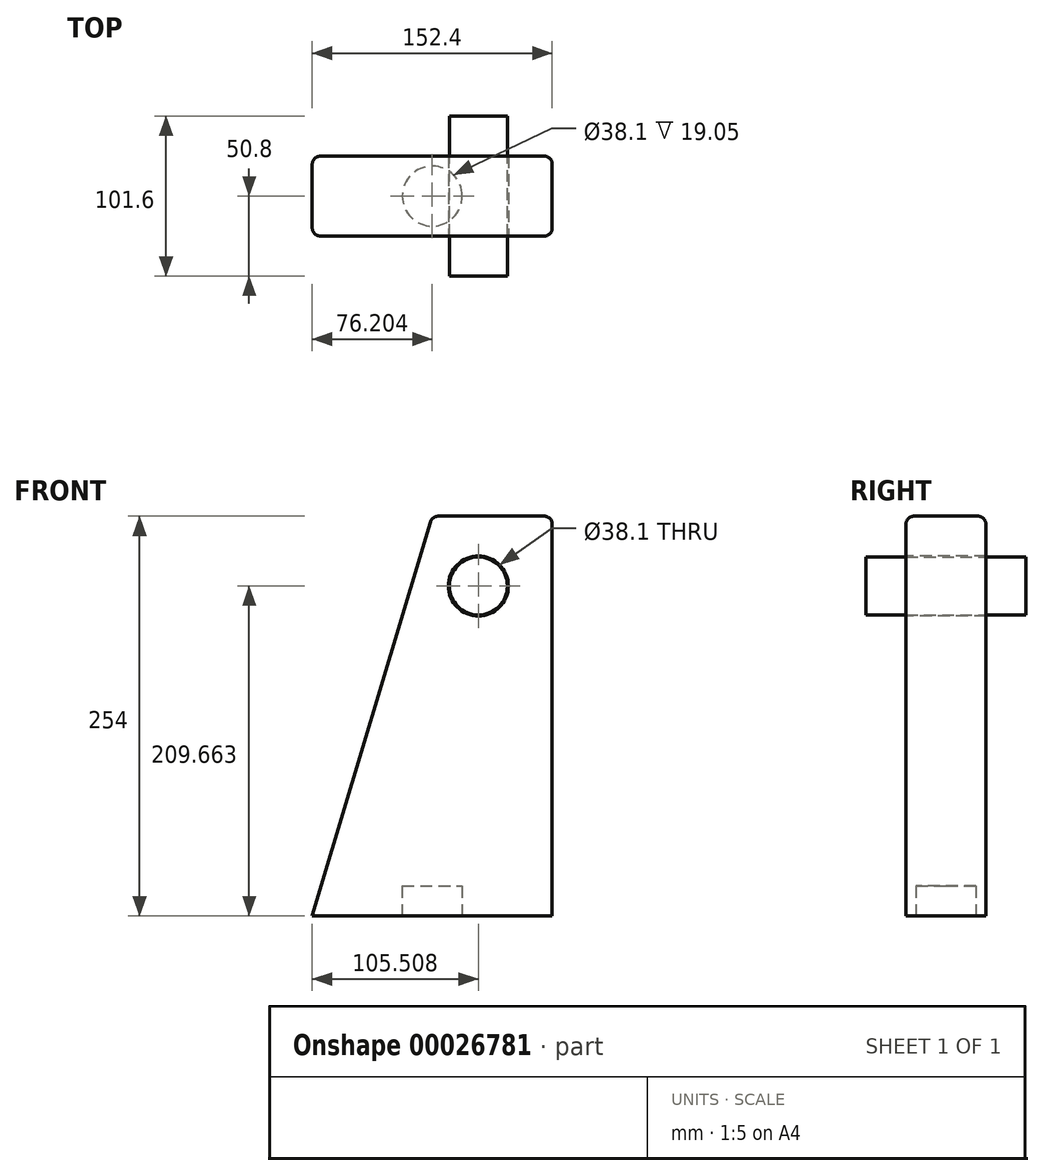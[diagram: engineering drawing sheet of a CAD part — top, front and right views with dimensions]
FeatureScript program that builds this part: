
annotation { "Feature Type Name" : "Feature", "Feature Type Description" : "" }
export const myFeature = defineFeature(function(context is Context, id is Id, definition is map)
    precondition{}
    {
        {
            var Q0;
            Q0=qCreatedBy(makeId("Front.planeOp"),FACE);
            var sketch = newSketch(context, id + "F0", { "sketchPlane" : qUnion([Q0])});
            skLineSegment(sketch, "E0", {"start": v(58.67, 124.9) * mm, "end": v(58.67, -129.1) * mm});
            skLineSegment(sketch, "E1", {"start": v(58.67, -129.1) * mm, "end": v(-93.73, -129.1) * mm});
            skLineSegment(sketch, "E2", {"start": v(-93.73, -129.1) * mm, "end": v(-17.53, 124.9) * mm});
            skLineSegment(sketch, "E3", {"start": v(-17.53, 124.9) * mm, "end": v(58.67, 124.9) * mm});
            skSolve(sketch);
        }
        {
            var Q0;
            Q0=makeQuery(id+"F0.imprint","IMPRINT",FACE,{"disambiguationData":[TD([[makeQuery(id+"F0.imprint","IMPRINT",EDGE,{"derivedFrom":sQuery(id+"F0.wireOp",EDGE,"E0")}),-1.0]])]});
            extrude(context, id + "F1", {"entities" : qUnion([Q0]), "depth" : 50.8 * mm});
        }
        {
            var Q0;
            Q0=makeQuery(id+"F1.opExtrude","SWEPT_FACE",FACE,{"disambiguationData":[OSD([sQuery(id+"F0.wireOp",EDGE,"E1")])]});
            var sketch = newSketch(context, id + "F2", { "sketchPlane" : qUnion([Q0])});
            skLineSegment(sketch, "E4", {"start": v(-17.53, 0) * mm, "end": v(-17.53, 25.4) * mm});
            skCircle(sketch, "E5", {"center": v(-17.53, 25.4) * mm, "radius": 19.05 * mm});
            skSolve(sketch);
        }
        {
            var Q0;
            Q0=makeQuery(id+"F2.imprint","IMPRINT",FACE,{"disambiguationData":[TD([[makeQuery(id+"F2.imprint","IMPRINT",EDGE,{"derivedFrom":sQuery(id+"F2.wireOp",EDGE,"E5")}),1.0]])]});
            extrude(context, id + "F3", {"entities" : qUnion([Q0]), "operationType" : NewBodyOperationType.REMOVE, "oppositeDirection" : true, "depth" : 19.05 * mm});
        }
        {
            var Q0;
            Q0=makeQuery(id+"F1.opExtrude","CAP_EDGE",EDGE,{"disambiguationData":[OSD([sQuery(id+"F0.wireOp",EDGE,"E2")])],"isStart":false});
            var Q1;
            Q1=makeQuery(id+"F1.opExtrude","CAP_EDGE",EDGE,{"disambiguationData":[OSD([sQuery(id+"F0.wireOp",EDGE,"E0")])],"isStart":false});
            var Q2;
            Q2=makeQuery(id+"F1.opExtrude","CAP_EDGE",EDGE,{"disambiguationData":[OSD([sQuery(id+"F0.wireOp",EDGE,"E0")])],"isStart":true});
            var Q3;
            Q3=makeQuery(id+"F1.opExtrude","CAP_EDGE",EDGE,{"disambiguationData":[OSD([sQuery(id+"F0.wireOp",EDGE,"E2")])],"isStart":true});
            var Q4;
            Q4=makeQuery(id+"F1.opExtrude","CAP_EDGE",EDGE,{"disambiguationData":[OSD([sQuery(id+"F0.wireOp",EDGE,"E3")])],"isStart":false});
            var Q5;
            Q5=makeQuery(id+"F1.opExtrude","SWEPT_EDGE",EDGE,{"disambiguationData":[OSD([sQuery(id+"F0.wireOp",EDGE,"E2"),sQuery(id+"F0.wireOp",EDGE,"E3")])]});
            var Q6;
            Q6=makeQuery(id+"F1.opExtrude","CAP_EDGE",EDGE,{"disambiguationData":[OSD([sQuery(id+"F0.wireOp",EDGE,"E3")])],"isStart":true});
            var Q7;
            Q7=makeQuery(id+"F1.opExtrude","SWEPT_EDGE",EDGE,{"disambiguationData":[OSD([sQuery(id+"F0.wireOp",EDGE,"E0"),sQuery(id+"F0.wireOp",EDGE,"E3")])]});
            fillet(context, id + "F4", {"entities" : qUnion([Q0, Q1, Q2, Q3, Q4, Q5, Q6, Q7]), "radius" : 5.08 * mm, "tangentPropagation" : true, "allowEdgeOverflow" : false});
        }
        {
            var Q0;
            Q0=makeQuery(id+"F1.opExtrude","CAP_FACE",FACE,{"disambiguationData":[OSD([sQuery(id+"F0.wireOp",EDGE,"E0"),sQuery(id+"F0.wireOp",EDGE,"E1"),sQuery(id+"F0.wireOp",EDGE,"E2"),sQuery(id+"F0.wireOp",EDGE,"E3")])],"isStart":false});
            var sketch = newSketch(context, id + "F5", { "sketchPlane" : qUnion([Q0])});
            skCircle(sketch, "E6", {"center": v(11.78, 80.56) * mm, "radius": 19.05 * mm});
            skSolve(sketch);
        }
        {
            var Q0;
            Q0 = qSketchRegion(id + "F5", true);
            extrude(context, id + "F6", {"entities" : qUnion([Q0]), "operationType" : NewBodyOperationType.REMOVE, "oppositeDirection" : true, "depth" : 50.8 * mm});
        }
        {
            var Q0;
            Q0=qCreatedBy(makeId("Front.planeOp"),FACE);
            cPlane(context, id + "F7", {"entities" : qUnion([Q0]), "cplaneType" : CPlaneType.OFFSET, "offset" : 25.4 * mm, "width" : 152.4 * mm, "height" : 152.4 * mm});
        }
        {
            var Q0;
            Q0=qCreatedBy(id+"F7.planeOp",FACE);
            var sketch = newSketch(context, id + "F8", { "sketchPlane" : qUnion([Q0])});
            skCircle(sketch, "E7", {"center": v(11.78, 80.56) * mm, "radius": 18.41 * mm});
            skSolve(sketch);
        }
        {
            var Q0;
            Q0 = qSketchRegion(id + "F8", true);
            extrude(context, id + "F9", {"entities" : qUnion([Q0]), "endBound" : BoundingType.SYMMETRIC, "depth" : 101.6 * mm});
        }
    });
